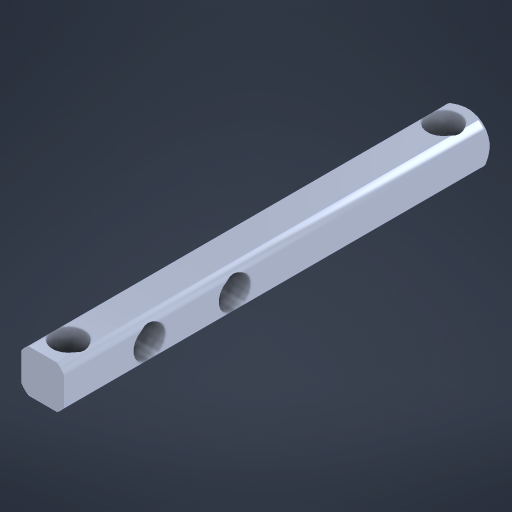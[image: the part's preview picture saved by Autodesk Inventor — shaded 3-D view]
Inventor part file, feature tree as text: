
AUTODESK INVENTOR PART (.ipt)
format: ipt  version: 2024 (Build 280153000, 153)  size: 346,112 bytes
history: native  units: in
note: dims shown in document units (in); Inventor stores cm internally (conversion verified against a paired STEP export)
features: other x50, sketch x4, extrude x2, hole x2, thicken_offset x1
ambient origin geometry x8: Origin, YZ Plane, XZ Plane, XY Plane, X Axis, Y Axis, Z Axis, Center Point
bodies: Solid1 (feature_tree)
feature tree (59):
  other  "Table"
  other  "Shaft HS 0.5 in"
  other  "Shaft HS 1.0 in"
  other  "Shaft HS 1.5 in"
  other  "Shaft HS 2.0 in"
  other  "Shaft HS 2.5 in"
  other  "Shaft HS 3.0 in"
  other  "Shaft HS 3.5 in"
  other  "Shaft HS 4.0 in"
  other  "Shaft HS 4.5 in"
  other  "Shaft HS 5.0 in"
  other  "Shaft HS 5.5 in"
  other  "Shaft HS 6.0 in"
  other  "Shaft HS 6.5 in"
  other  "Shaft HS 7.0 in"
  other  "Shaft HS 7.5 in"
  other  "Shaft HS 8.0 in"
  other  "Shaft HS 8.5 in"
  other  "Shaft HS 9.0 in"
  other  "Shaft HS 9.5 in"
  other  "Shaft HS 10.0 in"
  other  "Shaft HS 10.5 in"
  other  "Shaft HS 11.0 in"
  other  "Shaft HS 11.5 in"
  other  "Shaft HS 12.0 in"
  other  "Shaft HS 12.5 in"
  other  "Shaft HS 13.0 in"
  other  "Shaft HS 13.5 in"
  other  "Shaft HS 14.0 in"
  other  "Shaft HS 14.5 in"
  other  "Shaft HS 15.0 in"
  other  "Shaft HS 15.5 in"
  other  "Shaft HS 16.0 in"
  other  "Shaft HS 16.5 in"
  other  "Shaft HS 17.0 in"
  other  "Shaft HS 17.5 in"
  other  "Shaft HS 18.0 in"
  other  "Shaft HS 18.5 in"
  other  "Shaft HS 19.0 in"
  other  "Shaft HS 19.5 in"
  other  "Shaft HS 20.0 in"
  other  "Shaft HS 20.5 in"
  other  "Shaft HS 21.0 in"
  other  "Shaft HS 21.5 in"
  other  "Shaft HS 22.0 in"
  other  "Shaft HS 22.5 in"
  other  "Shaft HS 23.0 in"
  other  "Shaft HS 23.5 in"
  other  "Shaft HS 24.0 in"
  extrude  "Extrusion1"  Depth=12.1875in
  thicken_offset  "Thicken1"
  extrude  "Extrusion2"  Depth=21.625in
  hole  "Hole1"  [1 undecoded]
  hole  "Hole2"  [1 undecoded]
  sketch  "Sketch2"  dims[d0=0.0625in d1=0.0in d2=12.1875in]
  sketch  "Sketch3"  dims[d3=12.125in d4=21.625in]
  sketch  "Sketch6"  dims[d5=0.0in d9=0.15in]
  sketch  "Sketch7"  dims[d11=0.1875in d12=0.75in d13=0.375in d14=0.25in d15=0.5635in d16=1.0in d17=0.8108in d18=2.2in d20=0.5in d21=0.1875in d22=0.75in d23=0.375in d24=0.25in d25=0.5635in d26=1.0in d27=0.8108in d28=1.5in]
  other  "Cut-Revolve3"
note: 2 required parameter values undecoded (feature->parameter linkage not recoverable at this tier; creation-order binding heuristic only, values carry confidence <= 0.55)
